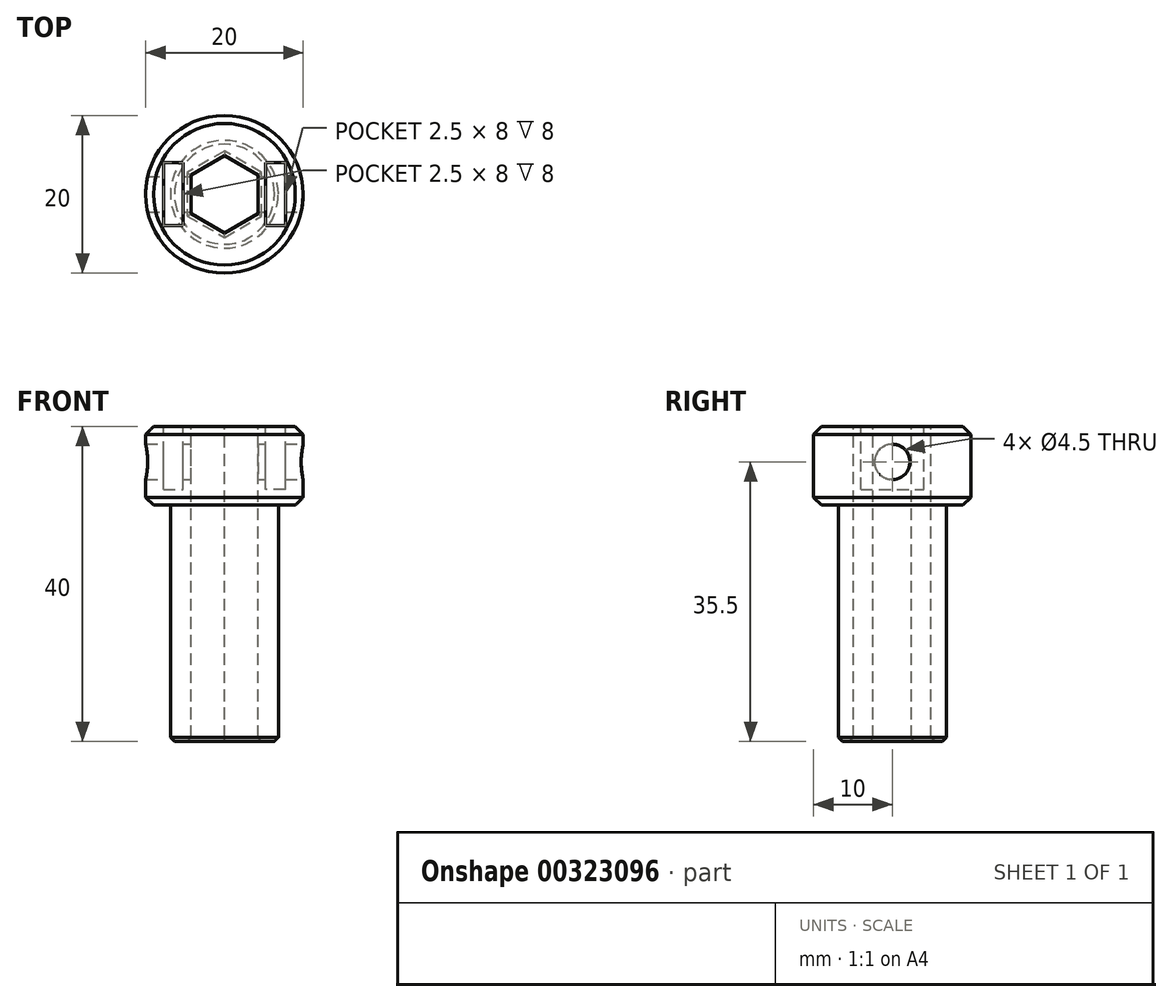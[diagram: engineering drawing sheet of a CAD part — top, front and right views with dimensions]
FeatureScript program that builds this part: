
annotation { "Feature Type Name" : "Feature", "Feature Type Description" : "" }
export const myFeature = defineFeature(function(context is Context, id is Id, definition is map)
    precondition{}
    {
        {
            var Q0;
            Q0=qCreatedBy(makeId("Front.planeOp"),FACE);
            var sketch = newSketch(context, id + "F0", { "sketchPlane" : qUnion([Q0])});
            skLineSegment(sketch, "E0", {"start": v(0, 0) * mm, "end": v(-6.85, 0) * mm});
            skLineSegment(sketch, "E1", {"start": v(-6.85, 0) * mm, "end": v(-6.85, 30) * mm});
            skLineSegment(sketch, "E2", {"start": v(-6.85, 30) * mm, "end": v(-10, 30) * mm});
            skLineSegment(sketch, "E3", {"start": v(-10, 30) * mm, "end": v(-10, 40) * mm});
            skLineSegment(sketch, "E4", {"start": v(-10, 40) * mm, "end": v(0, 40) * mm});
            skLineSegment(sketch, "E5", {"start": v(0, 40) * mm, "end": v(0, 0) * mm});
            skSolve(sketch);
        }
        {
            var Q0;
            Q0=makeQuery(id+"F0.imprint","IMPRINT",FACE,{"disambiguationData":[TD([[makeQuery(id+"F0.imprint","IMPRINT",EDGE,{"derivedFrom":sQuery(id+"F0.wireOp",EDGE,"E0")}),-1.0]])]});
            var Q1;
            Q1=sQuery(id+"F0.wireOp",EDGE,"E4");
            var Q2;
            Q2=sQuery(id+"F0.wireOp",EDGE,"E3");
            var Q3;
            Q3=sQuery(id+"F0.wireOp",EDGE,"E2");
            var Q4;
            Q4=sQuery(id+"F0.wireOp",EDGE,"E1");
            var Q5;
            Q5=sQuery(id+"F0.wireOp",EDGE,"E0");
            var Q6;
            Q6=sQuery(id+"F0.wireOp",EDGE,"E5");
            revolve(context, id + "F1", {"entities" : qUnion([Q0]), "surfaceEntities" : qUnion([Q1, Q2, Q3, Q4, Q5]), "axis" : qUnion([Q6]), "revolveType" : RevolveType.FULL});
        }
        {
            var Q0;
            Q0=makeQuery(id+"F1.opRevolve","SWEPT_FACE",FACE,{"disambiguationData":[OSD([sQuery(id+"F0.wireOp",EDGE,"E4")])]});
            var sketch = newSketch(context, id + "F2", { "sketchPlane" : qUnion([Q0])});
            skCircle(sketch, "E6.cCircle", {"center": v(0, 0) * mm, "radius": 4.25 * mm, "construction": true});
            skLineSegment(sketch, "E6.0", {"start": v(4.25, 2.45) * mm, "end": v(4.25, -2.45) * mm});
            skLineSegment(sketch, "E6.1", {"start": v(4.25, -2.45) * mm, "end": v(0, -4.9) * mm});
            skLineSegment(sketch, "E6.2", {"start": v(0, -4.9) * mm, "end": v(-4.25, -2.45) * mm});
            skLineSegment(sketch, "E6.3", {"start": v(-4.25, -2.45) * mm, "end": v(-4.25, 2.45) * mm});
            skLineSegment(sketch, "E6.4", {"start": v(-4.25, 2.45) * mm, "end": v(0, 4.9) * mm});
            skLineSegment(sketch, "E6.5", {"start": v(0, 4.9) * mm, "end": v(4.25, 2.45) * mm});
            skPoint(sketch, "E6.0.midPoint", {"position": v(4.25, 0) * mm});
            skLineSegment(sketch, "E7.bottom", {"start": v(-7.75, -4) * mm, "end": v(-5.25, -4) * mm});
            skLineSegment(sketch, "E7.top", {"start": v(-7.75, 4) * mm, "end": v(-5.25, 4) * mm});
            skLineSegment(sketch, "E7.left", {"start": v(-7.75, -4) * mm, "end": v(-7.75, 4) * mm});
            skLineSegment(sketch, "E7.right", {"start": v(-5.25, -4) * mm, "end": v(-5.25, 4) * mm});
            skPoint(sketch, "E8", {"position": v(-7.75, 0) * mm});
            skLineSegment(sketch, "E9.MirrorCS", {"start": v(7.75, -4) * mm, "end": v(7.75, 4) * mm});
            skLineSegment(sketch, "E10.MirrorCS", {"start": v(7.75, -4) * mm, "end": v(5.25, -4) * mm});
            skLineSegment(sketch, "E11.MirrorCS", {"start": v(5.25, -4) * mm, "end": v(5.25, 4) * mm});
            skLineSegment(sketch, "E12.MirrorCS", {"start": v(7.75, 4) * mm, "end": v(5.25, 4) * mm});
            skSolve(sketch);
        }
        {
            var Q0;
            Q0=makeQuery(id+"F2.imprint","IMPRINT",FACE,{"disambiguationData":[TD([[makeQuery(id+"F2.imprint","IMPRINT",EDGE,{"derivedFrom":sQuery(id+"F2.wireOp",EDGE,"E6.0")}),-1.0]])]});
            extrude(context, id + "F3", {"entities" : qUnion([Q0]), "operationType" : NewBodyOperationType.REMOVE, "endBound" : BoundingType.THROUGH_ALL, "oppositeDirection" : true, "depth" : 25 * mm});
        }
        {
            var Q0;
            Q0=makeQuery(id+"F2.imprint","IMPRINT",FACE,{"disambiguationData":[TD([[makeQuery(id+"F2.imprint","IMPRINT",EDGE,{"derivedFrom":sQuery(id+"F2.wireOp",EDGE,"E7.bottom")}),1.0]])]});
            var Q1;
            Q1=makeQuery(id+"F2.imprint","IMPRINT",FACE,{"disambiguationData":[TD([[makeQuery(id+"F2.imprint","IMPRINT",EDGE,{"derivedFrom":sQuery(id+"F2.wireOp",EDGE,"E9.MirrorCS")}),1.0]])]});
            extrude(context, id + "F4", {"entities" : qUnion([Q0, Q1]), "operationType" : NewBodyOperationType.REMOVE, "oppositeDirection" : true, "depth" : 8 * mm});
        }
        {
            var Q0;
            Q0=makeQuery(id+"F4.boolean.opBoolean","COPY",FACE,{"derivedFrom":makeQuery(id+"F4.opExtrude","SWEPT_FACE",FACE,{"disambiguationData":[OSD([sQuery(id+"F2.wireOp",EDGE,"E7.right")])]})});
            var sketch = newSketch(context, id + "F5", { "sketchPlane" : qUnion([Q0])});
            skCircle(sketch, "E13", {"center": v(0, 35.5) * mm, "radius": 2.25 * mm});
            skPoint(sketch, "E13.centerSnap0", {"position": v(0, 32) * mm});
            skSolve(sketch);
        }
        {
            var Q0;
            Q0=makeQuery(id+"F5.imprint","IMPRINT",FACE,{"disambiguationData":[TD([[makeQuery(id+"F5.imprint","IMPRINT",EDGE,{"derivedFrom":sQuery(id+"F5.wireOp",EDGE,"E13")}),1.0]])]});
            extrude(context, id + "F6", {"entities" : qUnion([Q0]), "operationType" : NewBodyOperationType.REMOVE, "endBound" : BoundingType.SYMMETRIC, "depth" : 50 * mm});
        }
        {
            var Q0;
            Q0=makeQuery(id+"F1.opRevolve","SWEPT_EDGE",EDGE,{"disambiguationData":[OSD([sQuery(id+"F0.wireOp",EDGE,"E3"),sQuery(id+"F0.wireOp",EDGE,"E4")])]});
            var Q1;
            Q1=makeQuery(id+"F1.opRevolve","SWEPT_EDGE",EDGE,{"disambiguationData":[OSD([sQuery(id+"F0.wireOp",EDGE,"E2"),sQuery(id+"F0.wireOp",EDGE,"E3")])]});
            var Q2;
            Q2=makeQuery(id+"F3.boolean.opBoolean","COPY",EDGE,{"derivedFrom":makeQuery(id+"F3.opExtrude","CAP_EDGE",EDGE,{"disambiguationData":[OSD([sQuery(id+"F2.wireOp",EDGE,"E6.4")])],"isStart":true})});
            var Q3;
            Q3=makeQuery(id+"F3.boolean.opBoolean","COPY",EDGE,{"derivedFrom":makeQuery(id+"F3.opExtrude","CAP_EDGE",EDGE,{"disambiguationData":[OSD([sQuery(id+"F2.wireOp",EDGE,"E6.5")])],"isStart":true})});
            var Q4;
            Q4=makeQuery(id+"F3.boolean.opBoolean","COPY",EDGE,{"derivedFrom":makeQuery(id+"F3.opExtrude","CAP_EDGE",EDGE,{"disambiguationData":[OSD([sQuery(id+"F2.wireOp",EDGE,"E6.0")])],"isStart":true})});
            var Q5;
            Q5=makeQuery(id+"F3.boolean.opBoolean","COPY",EDGE,{"derivedFrom":makeQuery(id+"F3.opExtrude","CAP_EDGE",EDGE,{"disambiguationData":[OSD([sQuery(id+"F2.wireOp",EDGE,"E6.1")])],"isStart":true})});
            var Q6;
            Q6=makeQuery(id+"F3.boolean.opBoolean","COPY",EDGE,{"derivedFrom":makeQuery(id+"F3.opExtrude","CAP_EDGE",EDGE,{"disambiguationData":[OSD([sQuery(id+"F2.wireOp",EDGE,"E6.2")])],"isStart":true})});
            var Q7;
            Q7=makeQuery(id+"F3.boolean.opBoolean","COPY",EDGE,{"derivedFrom":makeQuery(id+"F3.opExtrude","CAP_EDGE",EDGE,{"disambiguationData":[OSD([sQuery(id+"F2.wireOp",EDGE,"E6.3")])],"isStart":true})});
            chamfer(context, id + "F7", {"entities" : qUnion([Q0, Q1, Q2, Q3, Q4, Q5, Q6, Q7]), "width" : 1 * mm, "tangentPropagation" : true});
        }
        {
            var Q0;
            Q0=makeQuery(id+"F1.opRevolve","SWEPT_EDGE",EDGE,{"disambiguationData":[OSD([sQuery(id+"F0.wireOp",EDGE,"E0"),sQuery(id+"F0.wireOp",EDGE,"E1")])]});
            var Q1;
            Q1=makeQuery(id+"F3.boolean.opBoolean","INTERSECT",EDGE,{"derivedFrom":[makeQuery(id+"F1.opRevolve","SWEPT_FACE",FACE,{"disambiguationData":[OSD([sQuery(id+"F0.wireOp",EDGE,"E0")])]}),makeQuery(id+"F3.opExtrude","SWEPT_FACE",FACE,{"disambiguationData":[OSD([sQuery(id+"F2.wireOp",EDGE,"E6.0")])]})]});
            var Q2;
            Q2=makeQuery(id+"F3.boolean.opBoolean","INTERSECT",EDGE,{"derivedFrom":[makeQuery(id+"F1.opRevolve","SWEPT_FACE",FACE,{"disambiguationData":[OSD([sQuery(id+"F0.wireOp",EDGE,"E0")])]}),makeQuery(id+"F3.opExtrude","SWEPT_FACE",FACE,{"disambiguationData":[OSD([sQuery(id+"F2.wireOp",EDGE,"E6.1")])]})]});
            var Q3;
            Q3=makeQuery(id+"F3.boolean.opBoolean","INTERSECT",EDGE,{"derivedFrom":[makeQuery(id+"F1.opRevolve","SWEPT_FACE",FACE,{"disambiguationData":[OSD([sQuery(id+"F0.wireOp",EDGE,"E0")])]}),makeQuery(id+"F3.opExtrude","SWEPT_FACE",FACE,{"disambiguationData":[OSD([sQuery(id+"F2.wireOp",EDGE,"E6.2")])]})]});
            var Q4;
            Q4=makeQuery(id+"F3.boolean.opBoolean","INTERSECT",EDGE,{"derivedFrom":[makeQuery(id+"F1.opRevolve","SWEPT_FACE",FACE,{"disambiguationData":[OSD([sQuery(id+"F0.wireOp",EDGE,"E0")])]}),makeQuery(id+"F3.opExtrude","SWEPT_FACE",FACE,{"disambiguationData":[OSD([sQuery(id+"F2.wireOp",EDGE,"E6.3")])]})]});
            var Q5;
            Q5=makeQuery(id+"F3.boolean.opBoolean","INTERSECT",EDGE,{"derivedFrom":[makeQuery(id+"F1.opRevolve","SWEPT_FACE",FACE,{"disambiguationData":[OSD([sQuery(id+"F0.wireOp",EDGE,"E0")])]}),makeQuery(id+"F3.opExtrude","SWEPT_FACE",FACE,{"disambiguationData":[OSD([sQuery(id+"F2.wireOp",EDGE,"E6.4")])]})]});
            var Q6;
            Q6=makeQuery(id+"F3.boolean.opBoolean","INTERSECT",EDGE,{"derivedFrom":[makeQuery(id+"F1.opRevolve","SWEPT_FACE",FACE,{"disambiguationData":[OSD([sQuery(id+"F0.wireOp",EDGE,"E0")])]}),makeQuery(id+"F3.opExtrude","SWEPT_FACE",FACE,{"disambiguationData":[OSD([sQuery(id+"F2.wireOp",EDGE,"E6.5")])]})]});
            chamfer(context, id + "F8", {"entities" : qUnion([Q0, Q1, Q2, Q3, Q4, Q5, Q6]), "width" : 0.5 * mm, "tangentPropagation" : true});
        }
    });
